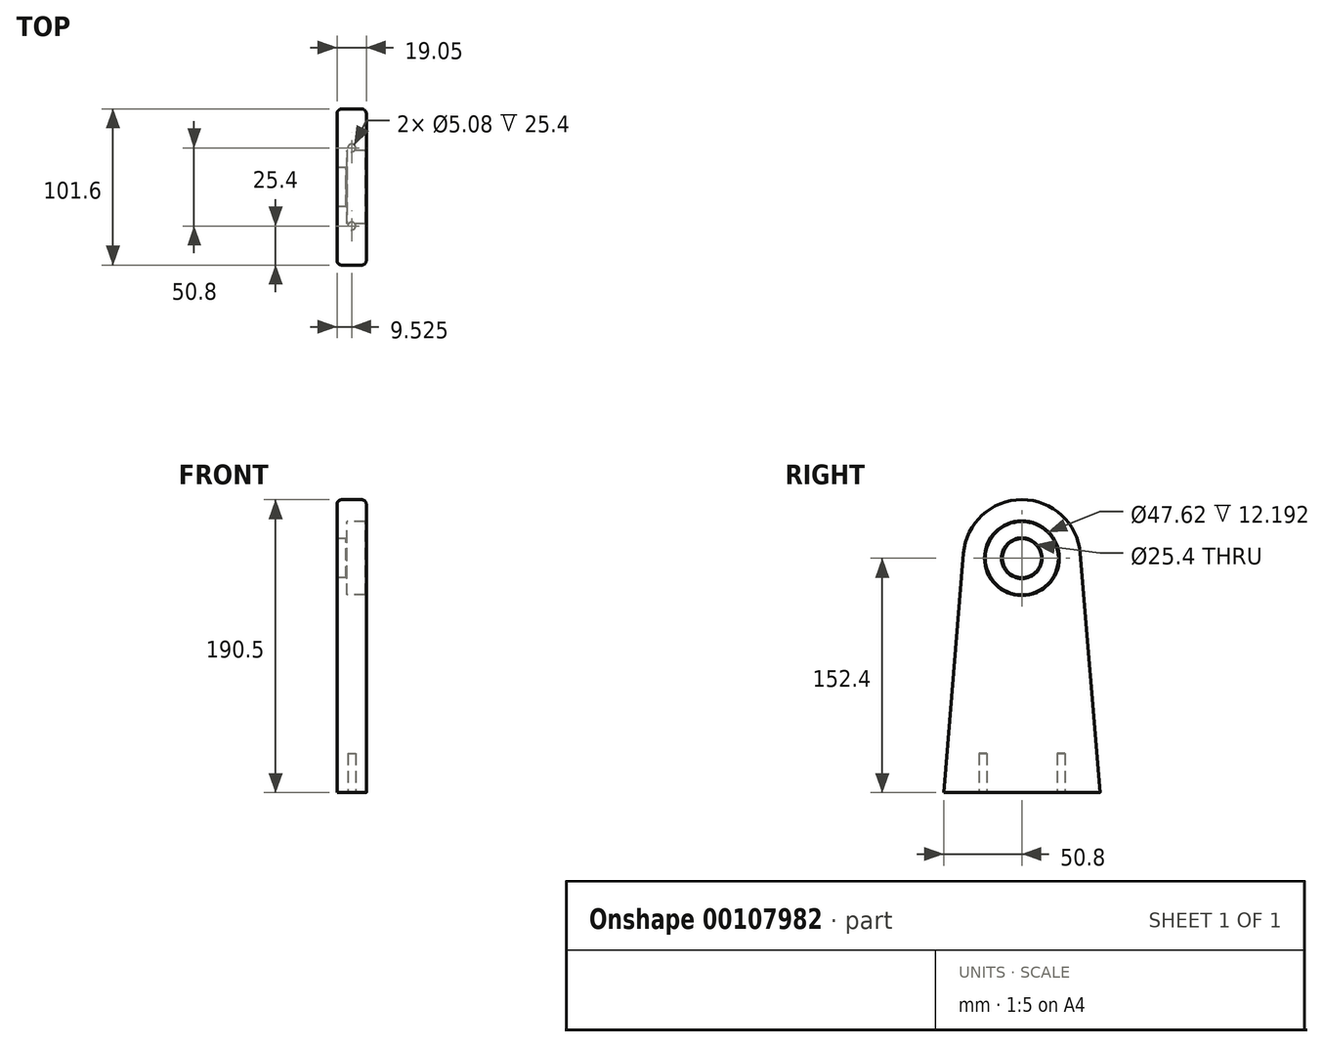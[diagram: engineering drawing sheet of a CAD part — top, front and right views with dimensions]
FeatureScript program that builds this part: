
annotation { "Feature Type Name" : "Feature", "Feature Type Description" : "" }
export const myFeature = defineFeature(function(context is Context, id is Id, definition is map)
    precondition{}
    {
        {
            var Q0;
            Q0=qCreatedBy(makeId("Right.planeOp"),FACE);
            var sketch = newSketch(context, id + "F0", { "sketchPlane" : qUnion([Q0])});
            skCircle(sketch, "E0", {"center": v(0, 0) * mm, "radius": 23.81 * mm});
            skArc(sketch, "E1", {"start": v(37.97, 3.13) * mm, "mid": v(0, 38.1) * mm, "end": v(-37.97, 3.13) * mm});
            skCircle(sketch, "E2", {"center": v(0, 0) * mm, "radius": 12.7 * mm});
            skLineSegment(sketch, "E3", {"start": v(-50.8, -152.4) * mm, "end": v(50.8, -152.4) * mm});
            skLineSegment(sketch, "E4", {"start": v(-50.8, -152.4) * mm, "end": v(-37.97, 3.13) * mm});
            skLineSegment(sketch, "E5", {"start": v(50.8, -152.4) * mm, "end": v(37.97, 3.13) * mm});
            skPoint(sketch, "E6.left.start.orphan", {"position": v(38.1, -152.4) * mm});
            skSolve(sketch);
        }
        {
            var Q0;
            Q0=makeQuery(id+"F0.imprint","IMPRINT",FACE,{"disambiguationData":[TD([[makeQuery(id+"F0.imprint","IMPRINT",EDGE,{"derivedFrom":sQuery(id+"F0.wireOp",EDGE,"E0")}),-1.0]])]});
            extrude(context, id + "F1", {"entities" : qUnion([Q0]), "depth" : 19.05 * mm});
        }
        {
            var Q0;
            Q0=makeQuery(id+"F0.imprint","IMPRINT",FACE,{"disambiguationData":[TD([[makeQuery(id+"F0.imprint","IMPRINT",EDGE,{"derivedFrom":sQuery(id+"F0.wireOp",EDGE,"E0")}),1.0]])]});
            extrude(context, id + "F2", {"entities" : qUnion([Q0]), "operationType" : NewBodyOperationType.ADD, "depth" : 6.35 * mm});
        }
        {
            var Q0;
            Q0=makeQuery(id+"F2.opExtrude","CAP_EDGE",EDGE,{"disambiguationData":[OSD([sQuery(id+"F0.wireOp",EDGE,"E2")])],"isStart":false});
            var Q1;
            Q1=makeQuery(id+"F1.opExtrude","CAP_EDGE",EDGE,{"disambiguationData":[OSD([sQuery(id+"F0.wireOp",EDGE,"E0")])],"isStart":false});
            var Q2;
            Q2=makeQuery(id+"F2.opExtrude","CAP_EDGE",EDGE,{"disambiguationData":[OSD([sQuery(id+"F0.wireOp",EDGE,"E2")])],"isStart":true});
            chamfer(context, id + "F3", {"entities" : qUnion([Q0, Q1, Q2]), "width" : 0.5 * mm, "tangentPropagation" : true});
        }
        {
            var Q0;
            Q0=makeQuery(id+"F1.opExtrude","SWEPT_FACE",FACE,{"disambiguationData":[OSD([sQuery(id+"F0.wireOp",EDGE,"E3")])]});
            var sketch = newSketch(context, id + "F4", { "sketchPlane" : qUnion([Q0])});
            skCircle(sketch, "E7", {"center": v(9.53, 25.4) * mm, "radius": 2.54 * mm});
            skCircle(sketch, "E8", {"center": v(9.53, -25.4) * mm, "radius": 2.54 * mm});
            skSolve(sketch);
        }
        {
            var Q0;
            Q0=makeQuery(id+"F4.imprint","IMPRINT",FACE,{"disambiguationData":[TD([[makeQuery(id+"F4.imprint","IMPRINT",EDGE,{"derivedFrom":sQuery(id+"F4.wireOp",EDGE,"E7")}),1.0]])]});
            var Q1;
            Q1=makeQuery(id+"F4.imprint","IMPRINT",FACE,{"disambiguationData":[TD([[makeQuery(id+"F4.imprint","IMPRINT",EDGE,{"derivedFrom":sQuery(id+"F4.wireOp",EDGE,"E8")}),1.0]])]});
            extrude(context, id + "F5", {"entities" : qUnion([Q0, Q1]), "operationType" : NewBodyOperationType.REMOVE, "oppositeDirection" : true, "depth" : 25.4 * mm});
        }
        {
            var Q0;
            Q0=makeQuery(id+"F1.opExtrude","CAP_EDGE",EDGE,{"disambiguationData":[OSD([sQuery(id+"F0.wireOp",EDGE,"E4")])],"isStart":false});
            var Q1;
            Q1=makeQuery(id+"F1.opExtrude","CAP_EDGE",EDGE,{"disambiguationData":[OSD([sQuery(id+"F0.wireOp",EDGE,"E4")])],"isStart":true});
            fillet(context, id + "F6", {"entities" : qUnion([Q0, Q1]), "radius" : 3.17 * mm, "tangentPropagation" : true, "allowEdgeOverflow" : false});
        }
    });
